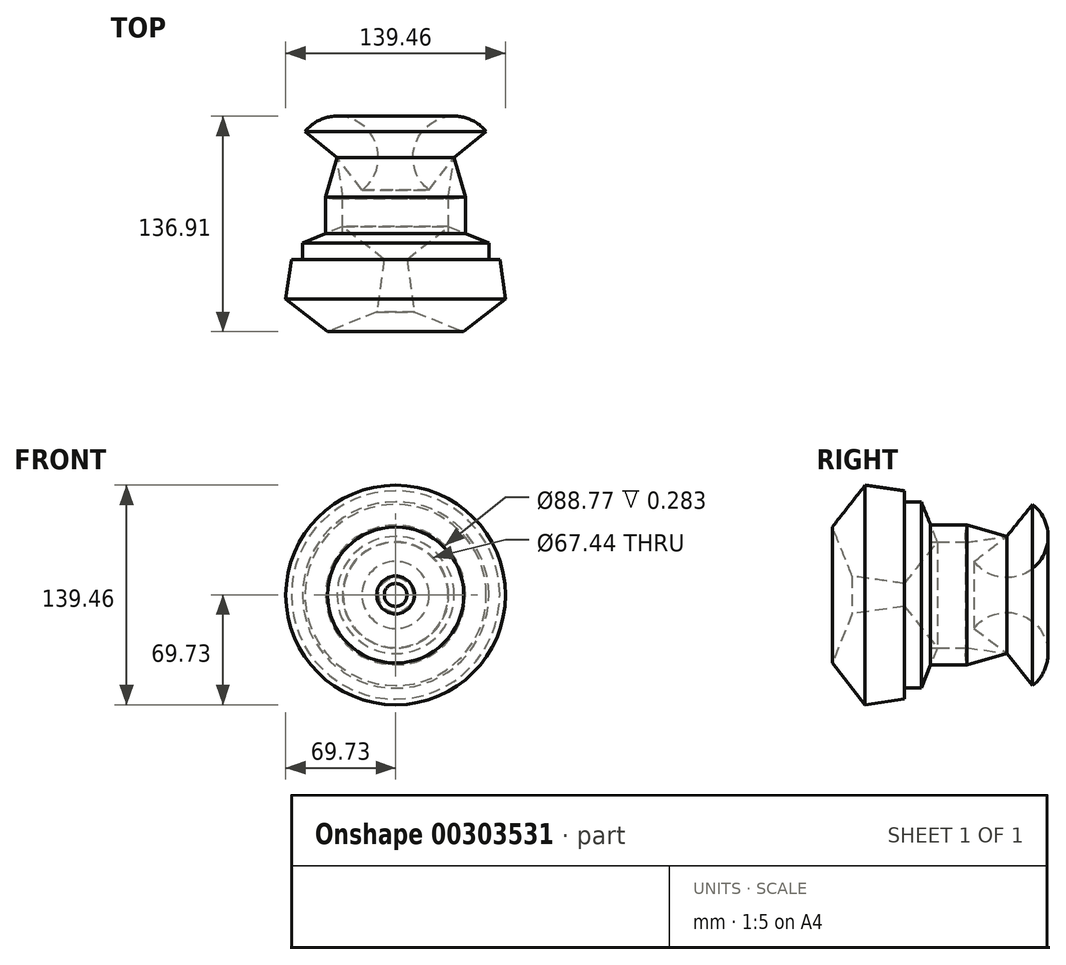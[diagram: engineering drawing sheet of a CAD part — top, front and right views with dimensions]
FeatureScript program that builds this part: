
annotation { "Feature Type Name" : "Feature", "Feature Type Description" : "" }
export const myFeature = defineFeature(function(context is Context, id is Id, definition is map)
    precondition{}
    {
        {
            var Q0;
            Q0=qCreatedBy(makeId("Top.planeOp"),FACE);
            var sketch = newSketch(context, id + "F0", { "sketchPlane" : qUnion([Q0])});
            skArc(sketch, "E0", {"start": v(57.57, 55.18) * mm, "mid": v(18.43, 57.05) * mm, "end": v(21.29, 17.97) * mm});
            skLineSegment(sketch, "E1", {"start": v(0, 60.84) * mm, "end": v(0, 18.44) * mm});
            skLineSegment(sketch, "E2", {"start": v(44.39, 13.6) * mm, "end": v(37.17, 38.77) * mm});
            skLineSegment(sketch, "E3", {"start": v(37.17, 38.77) * mm, "end": v(57.57, 55.18) * mm});
            skLineSegment(sketch, "E4", {"start": v(21.29, 17.97) * mm, "end": v(37.17, 38.77) * mm});
            skLineSegment(sketch, "E5", {"start": v(37.17, 38.77) * mm, "end": v(33.35, 12.87) * mm});
            skArc(sketch, "E6.trimOffspring", {"start": v(33.35, 12.87) * mm, "mid": v(38.9, 12.65) * mm, "end": v(44.39, 13.6) * mm});
            skArc(sketch, "E7.cCircle", {"start": v(59.17, -18.07) * mm, "mid": v(14.62, -55.4) * mm, "end": v(64.83, -26.13) * mm, "construction": true});
            skLineSegment(sketch, "E7.0", {"start": v(69.73, -51.17) * mm, "end": v(43.24, -71.96) * mm});
            skLineSegment(sketch, "E7.1", {"start": v(43.24, -71.96) * mm, "end": v(11.99, -59.42) * mm});
            skLineSegment(sketch, "E7.2", {"start": v(11.99, -59.42) * mm, "end": v(7.23, -26.08) * mm});
            skLineSegment(sketch, "E7.3", {"start": v(7.23, -26.08) * mm, "end": v(33.72, -5.29) * mm});
            skLineSegment(sketch, "E7.4", {"start": v(33.72, -5.29) * mm, "end": v(59.17, -15.5) * mm});
            skLineSegment(sketch, "E7.5", {"start": v(66.16, -26.13) * mm, "end": v(69.73, -51.17) * mm});
            skPoint(sketch, "E7.0.midPoint", {"position": v(56.49, -61.57) * mm});
            skLineSegment(sketch, "E8.bottom", {"start": v(66.16, -26.13) * mm, "end": v(59.17, -26.13) * mm});
            skLineSegment(sketch, "E8.right", {"start": v(59.17, -26.13) * mm, "end": v(59.17, -15.5) * mm});
            skPoint(sketch, "E9.orphan", {"position": v(64.97, -17.83) * mm});
            skLineSegment(sketch, "E10.bottom", {"start": v(44.39, 13.6) * mm, "end": v(33.72, 13.6) * mm});
            skLineSegment(sketch, "E10.top", {"start": v(44.39, -9.85) * mm, "end": v(33.72, -9.85) * mm});
            skLineSegment(sketch, "E10.left", {"start": v(44.39, 13.6) * mm, "end": v(44.39, -9.85) * mm});
            skLineSegment(sketch, "E10.right", {"start": v(33.72, 13.6) * mm, "end": v(33.72, -9.85) * mm});
            skSolve(sketch);
        }
        {
            var Q0;
            Q0=makeQuery(id+"F0.imprint","IMPRINT",FACE,{"disambiguationData":[TD([[makeQuery(id+"F0.imprint","IMPRINT",EDGE,{"derivedFrom":sQuery(id+"F0.wireOp",EDGE,"E0")}),1.0]])]});
            var Q1;
            Q1=makeQuery(id+"F0.imprint","IMPRINT",FACE,{"disambiguationData":[TD([[makeQuery(id+"F0.imprint","IMPRINT",EDGE,{"derivedFrom":sQuery(id+"F0.wireOp",EDGE,"E2")}),1.0]])]});
            var Q2;
            Q2=makeQuery(id+"F0.imprint","IMPRINT",FACE,{"disambiguationData":[TD([[makeQuery(id+"F0.imprint","IMPRINT",EDGE,{"derivedFrom":sQuery(id+"F0.wireOp",EDGE,"E7.0")}),-1.0]])]});
            var Q3;
            {var subQ0=sQuery(id+"F0.wireOp",EDGE,"E10.left");var subQ5=sQuery(id+"F0.wireOp",EDGE,"E7.4");var subQ7=makeQuery(id+"F0.imprint","INTERSECT",VERTEX,{"derivedFrom":[subQ5,subQ0]});Q3=makeQuery(id+"F0.imprint","IMPRINT",FACE,{"disambiguationData":[TD([[makeQuery(id+"F0.imprint","IMPRINT",EDGE,{"disambiguationData":[TD([[subQ7,1.0]])],"derivedFrom":subQ5}),1.0]])]});}
            var Q4;
            Q4=sQuery(id+"F0.wireOp",EDGE,"E1");
            revolve(context, id + "F1", {"entities" : qUnion([Q0, Q1, Q2, Q3]), "axis" : qUnion([Q4]), "revolveType" : RevolveType.FULL});
        }
    });
